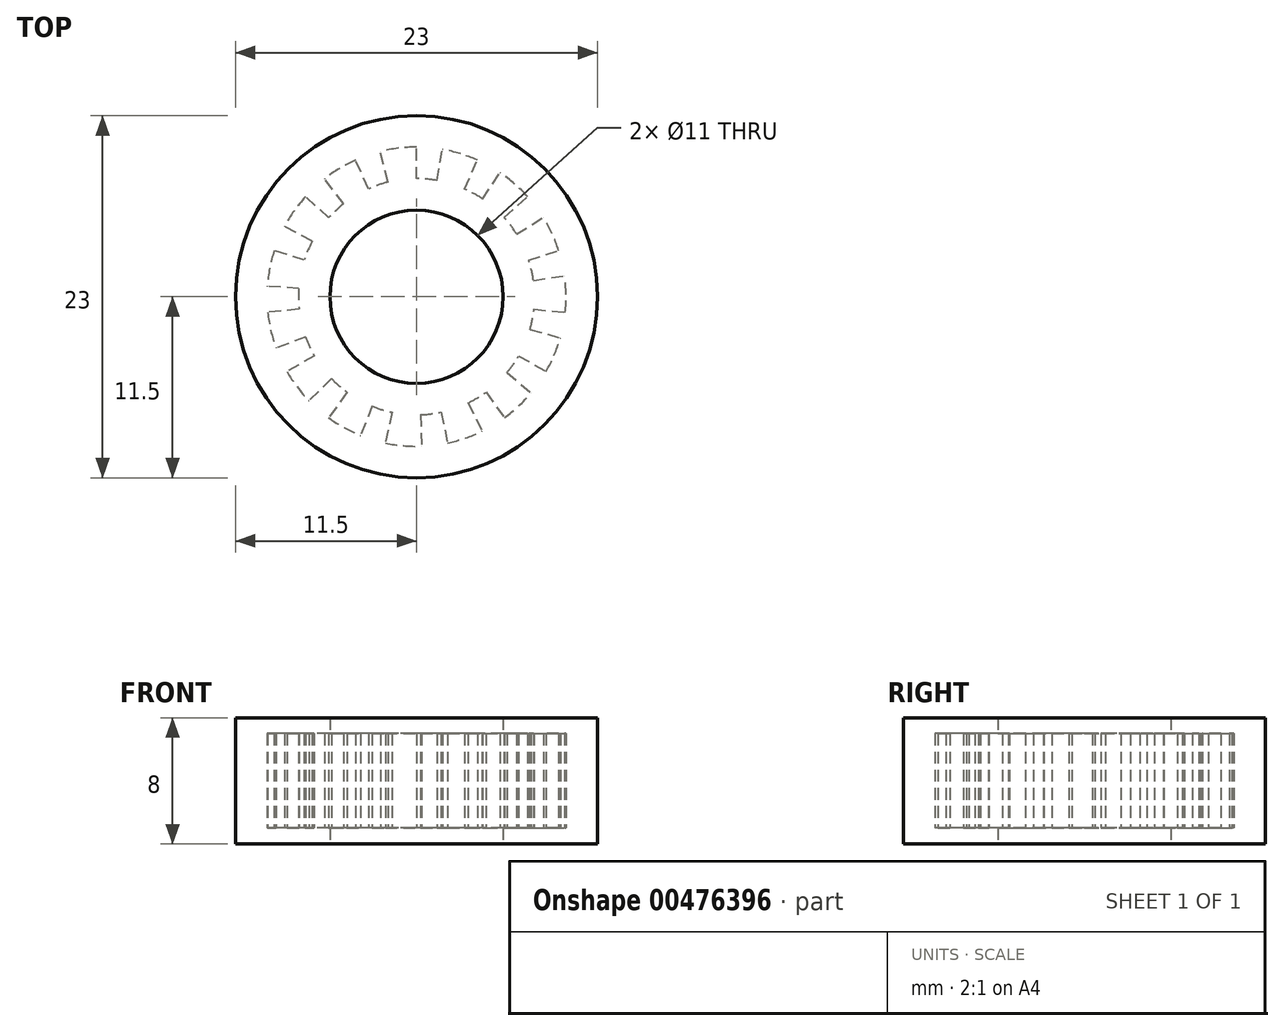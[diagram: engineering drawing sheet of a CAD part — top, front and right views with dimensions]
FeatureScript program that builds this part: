
annotation { "Feature Type Name" : "Feature", "Feature Type Description" : "" }
export const myFeature = defineFeature(function(context is Context, id is Id, definition is map)
    precondition{}
    {
        {
            var Q0;
            Q0=qCreatedBy(makeId("Top.planeOp"),FACE);
            var sketch = newSketch(context, id + "F0", { "sketchPlane" : qUnion([Q0])});
            skCircle(sketch, "E0", {"center": v(0, 0) * mm, "radius": 11.5 * mm});
            skCircle(sketch, "E1", {"center": v(0, 0) * mm, "radius": 5.5 * mm});
            skSolve(sketch);
        }
        {
            var Q0;
            Q0=makeQuery(id+"F0.imprint","IMPRINT",FACE,{"disambiguationData":[TD([[makeQuery(id+"F0.imprint","IMPRINT",EDGE,{"derivedFrom":sQuery(id+"F0.wireOp",EDGE,"E0")}),1.0]])]});
            extrude(context, id + "F1", {"entities" : qUnion([Q0]), "depth" : 1 * mm});
        }
        {
            var Q0;
            Q0=makeQuery(id+"F1.opExtrude","CAP_FACE",FACE,{"disambiguationData":[OSD([sQuery(id+"F0.wireOp",EDGE,"E0"),sQuery(id+"F0.wireOp",EDGE,"E1")])],"isStart":false});
            var sketch = newSketch(context, id + "F2", { "sketchPlane" : qUnion([Q0])});
            skCircle(sketch, "E2", {"center": v(0, 0) * mm, "radius": 11.5 * mm});
            skLineSegment(sketch, "E3", {"start": v(0, 0) * mm, "end": v(0, 7.5) * mm, "construction": true});
            skLineSegment(sketch, "E4", {"start": v(0, 7.5) * mm, "end": v(0, 9.5) * mm});
            skLineSegment(sketch, "E5", {"start": v(0, 0) * mm, "end": v(-1.81, 7.28) * mm, "construction": true});
            skLineSegment(sketch, "E6", {"start": v(-1.81, 7.28) * mm, "end": v(-2.3, 9.22) * mm});
            skLineSegment(sketch, "E7", {"start": v(0, 0) * mm, "end": v(-3.05, 6.85) * mm, "construction": true});
            skArc(sketch, "E8", {"start": v(0, 9.5) * mm, "mid": v(-1.16, 9.43) * mm, "end": v(-2.3, 9.22) * mm});
            skArc(sketch, "E9", {"start": v(-1.81, 7.28) * mm, "mid": v(-2.44, 7.1) * mm, "end": v(-3.05, 6.85) * mm});
            skArc(sketch, "E10.1.0", {"start": v(-4.62, 5.91) * mm, "mid": v(-5.11, 5.49) * mm, "end": v(-5.57, 5.02) * mm});
            skLineSegment(sketch, "E10.1.1", {"start": v(-4.62, 5.91) * mm, "end": v(-5.85, 7.49) * mm});
            skArc(sketch, "E10.1.2", {"start": v(-3.86, 8.68) * mm, "mid": v(-4.9, 8.14) * mm, "end": v(-5.85, 7.49) * mm});
            skLineSegment(sketch, "E10.1.3", {"start": v(-3.05, 6.85) * mm, "end": v(-3.86, 8.68) * mm});
            skArc(sketch, "E10.2.0", {"start": v(-6.62, 3.52) * mm, "mid": v(-6.9, 2.93) * mm, "end": v(-7.13, 2.32) * mm});
            skLineSegment(sketch, "E10.2.1", {"start": v(-6.62, 3.52) * mm, "end": v(-8.39, 4.46) * mm});
            skArc(sketch, "E10.2.2", {"start": v(-7.06, 6.36) * mm, "mid": v(-7.78, 5.45) * mm, "end": v(-8.39, 4.46) * mm});
            skLineSegment(sketch, "E10.2.3", {"start": v(-5.57, 5.02) * mm, "end": v(-7.06, 6.36) * mm});
            skArc(sketch, "E10.3.0", {"start": v(-7.48, 0.52) * mm, "mid": v(-7.5, -0.13) * mm, "end": v(-7.46, -0.78) * mm});
            skLineSegment(sketch, "E10.3.1", {"start": v(-7.48, 0.52) * mm, "end": v(-9.48, 0.66) * mm});
            skArc(sketch, "E10.3.2", {"start": v(-9.04, 2.94) * mm, "mid": v(-9.33, 1.81) * mm, "end": v(-9.48, 0.66) * mm});
            skLineSegment(sketch, "E10.3.3", {"start": v(-7.13, 2.32) * mm, "end": v(-9.04, 2.94) * mm});
            skArc(sketch, "E10.4.0", {"start": v(-7.05, -2.57) * mm, "mid": v(-6.8, -3.17) * mm, "end": v(-6.5, -3.75) * mm});
            skLineSegment(sketch, "E10.4.1", {"start": v(-7.05, -2.57) * mm, "end": v(-8.93, -3.25) * mm});
            skArc(sketch, "E10.4.2", {"start": v(-9.45, -1) * mm, "mid": v(-9.26, -2.14) * mm, "end": v(-8.93, -3.25) * mm});
            skLineSegment(sketch, "E10.4.3", {"start": v(-7.46, -0.78) * mm, "end": v(-9.45, -1) * mm});
            skArc(sketch, "E10.5.0", {"start": v(-5.4, -5.2) * mm, "mid": v(-4.92, -5.66) * mm, "end": v(-4.4, -6.07) * mm});
            skLineSegment(sketch, "E10.5.1", {"start": v(-5.4, -5.2) * mm, "end": v(-6.83, -6.6) * mm});
            skArc(sketch, "E10.5.2", {"start": v(-8.23, -4.75) * mm, "mid": v(-7.59, -5.72) * mm, "end": v(-6.83, -6.6) * mm});
            skLineSegment(sketch, "E10.5.3", {"start": v(-6.5, -3.75) * mm, "end": v(-8.23, -4.75) * mm});
            skArc(sketch, "E10.6.0", {"start": v(-2.8, -6.95) * mm, "mid": v(-2.2, -7.17) * mm, "end": v(-1.56, -7.34) * mm});
            skLineSegment(sketch, "E10.6.1", {"start": v(-2.8, -6.95) * mm, "end": v(-3.56, -8.8) * mm});
            skArc(sketch, "E10.6.2", {"start": v(-5.58, -7.69) * mm, "mid": v(-4.6, -8.3) * mm, "end": v(-3.56, -8.8) * mm});
            skLineSegment(sketch, "E10.6.3", {"start": v(-4.4, -6.07) * mm, "end": v(-5.58, -7.69) * mm});
            skArc(sketch, "E10.7.0", {"start": v(0.26, -7.5) * mm, "mid": v(0.91, -7.44) * mm, "end": v(1.56, -7.34) * mm});
            skLineSegment(sketch, "E10.7.1", {"start": v(0.26, -7.5) * mm, "end": v(0.33, -9.5) * mm});
            skArc(sketch, "E10.7.2", {"start": v(-1.98, -9.3) * mm, "mid": v(-0.83, -9.46) * mm, "end": v(0.33, -9.5) * mm});
            skLineSegment(sketch, "E10.7.3", {"start": v(-1.56, -7.34) * mm, "end": v(-1.98, -9.3) * mm});
            skArc(sketch, "E10.8.0", {"start": v(3.29, -6.74) * mm, "mid": v(3.86, -6.43) * mm, "end": v(4.4, -6.07) * mm});
            skLineSegment(sketch, "E10.8.1", {"start": v(3.29, -6.74) * mm, "end": v(4.16, -8.54) * mm});
            skArc(sketch, "E10.8.2", {"start": v(1.98, -9.3) * mm, "mid": v(3.1, -8.98) * mm, "end": v(4.16, -8.54) * mm});
            skLineSegment(sketch, "E10.8.3", {"start": v(1.56, -7.34) * mm, "end": v(1.98, -9.3) * mm});
            skArc(sketch, "E10.9.0", {"start": v(5.75, -4.82) * mm, "mid": v(6.14, -4.3) * mm, "end": v(6.5, -3.75) * mm});
            skLineSegment(sketch, "E10.9.1", {"start": v(5.75, -4.82) * mm, "end": v(7.28, -6.1) * mm});
            skArc(sketch, "E10.9.2", {"start": v(5.58, -7.69) * mm, "mid": v(6.48, -6.95) * mm, "end": v(7.28, -6.1) * mm});
            skLineSegment(sketch, "E10.9.3", {"start": v(4.4, -6.07) * mm, "end": v(5.58, -7.69) * mm});
            skArc(sketch, "E10.10.0", {"start": v(7.2, -2.07) * mm, "mid": v(7.36, -1.43) * mm, "end": v(7.46, -0.78) * mm});
            skLineSegment(sketch, "E10.10.1", {"start": v(7.2, -2.07) * mm, "end": v(9.13, -2.62) * mm});
            skArc(sketch, "E10.10.2", {"start": v(8.23, -4.75) * mm, "mid": v(8.74, -3.71) * mm, "end": v(9.13, -2.62) * mm});
            skLineSegment(sketch, "E10.10.3", {"start": v(6.5, -3.75) * mm, "end": v(8.23, -4.75) * mm});
            skArc(sketch, "E10.11.0", {"start": v(7.43, 1.04) * mm, "mid": v(7.3, 1.69) * mm, "end": v(7.13, 2.32) * mm});
            skLineSegment(sketch, "E10.11.1", {"start": v(7.43, 1.04) * mm, "end": v(9.4, 1.32) * mm});
            skArc(sketch, "E10.11.2", {"start": v(9.45, -1) * mm, "mid": v(9.5, 0.17) * mm, "end": v(9.4, 1.32) * mm});
            skLineSegment(sketch, "E10.11.3", {"start": v(7.46, -0.78) * mm, "end": v(9.45, -1) * mm});
            skArc(sketch, "E10.12.0", {"start": v(6.36, 3.97) * mm, "mid": v(5.99, 4.51) * mm, "end": v(5.57, 5.02) * mm});
            skLineSegment(sketch, "E10.12.1", {"start": v(6.36, 3.97) * mm, "end": v(8.06, 5.03) * mm});
            skArc(sketch, "E10.12.2", {"start": v(9.04, 2.94) * mm, "mid": v(8.6, 4.01) * mm, "end": v(8.06, 5.03) * mm});
            skLineSegment(sketch, "E10.12.3", {"start": v(7.13, 2.32) * mm, "end": v(9.04, 2.94) * mm});
            skArc(sketch, "E10.13.0", {"start": v(4.2, 6.22) * mm, "mid": v(3.64, 6.56) * mm, "end": v(3.05, 6.85) * mm});
            skLineSegment(sketch, "E10.13.1", {"start": v(4.2, 6.22) * mm, "end": v(5.31, 7.88) * mm});
            skArc(sketch, "E10.13.2", {"start": v(7.06, 6.36) * mm, "mid": v(6.23, 7.17) * mm, "end": v(5.31, 7.88) * mm});
            skLineSegment(sketch, "E10.13.3", {"start": v(5.57, 5.02) * mm, "end": v(7.06, 6.36) * mm});
            skArc(sketch, "E10.14.0", {"start": v(1.3, 7.39) * mm, "mid": v(0.65, 7.47) * mm, "end": v(0, 7.5) * mm});
            skLineSegment(sketch, "E10.14.1", {"start": v(1.3, 7.39) * mm, "end": v(1.65, 9.36) * mm});
            skArc(sketch, "E10.14.2", {"start": v(3.86, 8.68) * mm, "mid": v(2.78, 9.08) * mm, "end": v(1.65, 9.36) * mm});
            skLineSegment(sketch, "E10.14.3", {"start": v(3.05, 6.85) * mm, "end": v(3.86, 8.68) * mm});
            skSolve(sketch);
        }
        {
            var Q0;
            Q0=makeQuery(id+"F2.imprint","IMPRINT",FACE,{"disambiguationData":[TD([[makeQuery(id+"F2.imprint","IMPRINT",EDGE,{"derivedFrom":sQuery(id+"F2.wireOp",EDGE,"E2")}),1.0]])]});
            extrude(context, id + "F3", {"entities" : qUnion([Q0]), "operationType" : NewBodyOperationType.ADD, "depth" : 6 * mm});
        }
        {
            var Q0;
            Q0=makeQuery(id+"F3.opExtrude","CAP_FACE",FACE,{"disambiguationData":[OSD([sQuery(id+"F2.wireOp",EDGE,"E2"),sQuery(id+"F2.wireOp",EDGE,"E4"),sQuery(id+"F2.wireOp",EDGE,"E6"),sQuery(id+"F2.wireOp",EDGE,"E8"),sQuery(id+"F2.wireOp",EDGE,"E9"),sQuery(id+"F2.wireOp",EDGE,"E10.1.0"),sQuery(id+"F2.wireOp",EDGE,"E10.1.1"),sQuery(id+"F2.wireOp",EDGE,"E10.1.2"),sQuery(id+"F2.wireOp",EDGE,"E10.1.3"),sQuery(id+"F2.wireOp",EDGE,"E10.2.0"),sQuery(id+"F2.wireOp",EDGE,"E10.2.1"),sQuery(id+"F2.wireOp",EDGE,"E10.2.2"),sQuery(id+"F2.wireOp",EDGE,"E10.2.3"),sQuery(id+"F2.wireOp",EDGE,"E10.3.0"),sQuery(id+"F2.wireOp",EDGE,"E10.3.1"),sQuery(id+"F2.wireOp",EDGE,"E10.3.2"),sQuery(id+"F2.wireOp",EDGE,"E10.3.3"),sQuery(id+"F2.wireOp",EDGE,"E10.4.0"),sQuery(id+"F2.wireOp",EDGE,"E10.4.1"),sQuery(id+"F2.wireOp",EDGE,"E10.4.2"),sQuery(id+"F2.wireOp",EDGE,"E10.4.3"),sQuery(id+"F2.wireOp",EDGE,"E10.5.0"),sQuery(id+"F2.wireOp",EDGE,"E10.5.1"),sQuery(id+"F2.wireOp",EDGE,"E10.5.2"),sQuery(id+"F2.wireOp",EDGE,"E10.5.3"),sQuery(id+"F2.wireOp",EDGE,"E10.6.0"),sQuery(id+"F2.wireOp",EDGE,"E10.6.1"),sQuery(id+"F2.wireOp",EDGE,"E10.6.2"),sQuery(id+"F2.wireOp",EDGE,"E10.6.3"),sQuery(id+"F2.wireOp",EDGE,"E10.7.0"),sQuery(id+"F2.wireOp",EDGE,"E10.7.1"),sQuery(id+"F2.wireOp",EDGE,"E10.7.2"),sQuery(id+"F2.wireOp",EDGE,"E10.7.3"),sQuery(id+"F2.wireOp",EDGE,"E10.8.0"),sQuery(id+"F2.wireOp",EDGE,"E10.8.1"),sQuery(id+"F2.wireOp",EDGE,"E10.8.2"),sQuery(id+"F2.wireOp",EDGE,"E10.8.3"),sQuery(id+"F2.wireOp",EDGE,"E10.9.0"),sQuery(id+"F2.wireOp",EDGE,"E10.9.1"),sQuery(id+"F2.wireOp",EDGE,"E10.9.2"),sQuery(id+"F2.wireOp",EDGE,"E10.9.3"),sQuery(id+"F2.wireOp",EDGE,"E10.10.0"),sQuery(id+"F2.wireOp",EDGE,"E10.10.1"),sQuery(id+"F2.wireOp",EDGE,"E10.10.2"),sQuery(id+"F2.wireOp",EDGE,"E10.10.3"),sQuery(id+"F2.wireOp",EDGE,"E10.11.0"),sQuery(id+"F2.wireOp",EDGE,"E10.11.1"),sQuery(id+"F2.wireOp",EDGE,"E10.11.2"),sQuery(id+"F2.wireOp",EDGE,"E10.11.3"),sQuery(id+"F2.wireOp",EDGE,"E10.12.0"),sQuery(id+"F2.wireOp",EDGE,"E10.12.1"),sQuery(id+"F2.wireOp",EDGE,"E10.12.2"),sQuery(id+"F2.wireOp",EDGE,"E10.12.3"),sQuery(id+"F2.wireOp",EDGE,"E10.13.0"),sQuery(id+"F2.wireOp",EDGE,"E10.13.1"),sQuery(id+"F2.wireOp",EDGE,"E10.13.2"),sQuery(id+"F2.wireOp",EDGE,"E10.13.3"),sQuery(id+"F2.wireOp",EDGE,"E10.14.0"),sQuery(id+"F2.wireOp",EDGE,"E10.14.1"),sQuery(id+"F2.wireOp",EDGE,"E10.14.2"),sQuery(id+"F2.wireOp",EDGE,"E10.14.3")])],"isStart":false});
            var sketch = newSketch(context, id + "F4", { "sketchPlane" : qUnion([Q0])});
            skCircle(sketch, "E11", {"center": v(0, 0) * mm, "radius": 5.5 * mm});
            skCircle(sketch, "E12", {"center": v(0, 0) * mm, "radius": 11.5 * mm});
            skSolve(sketch);
        }
        {
            var Q0;
            Q0=qSketchRegion(id+"F4",true);
            extrude(context, id + "F5", {"entities" : qUnion([Q0]), "operationType" : NewBodyOperationType.ADD, "depth" : 1 * mm});
        }
    });
